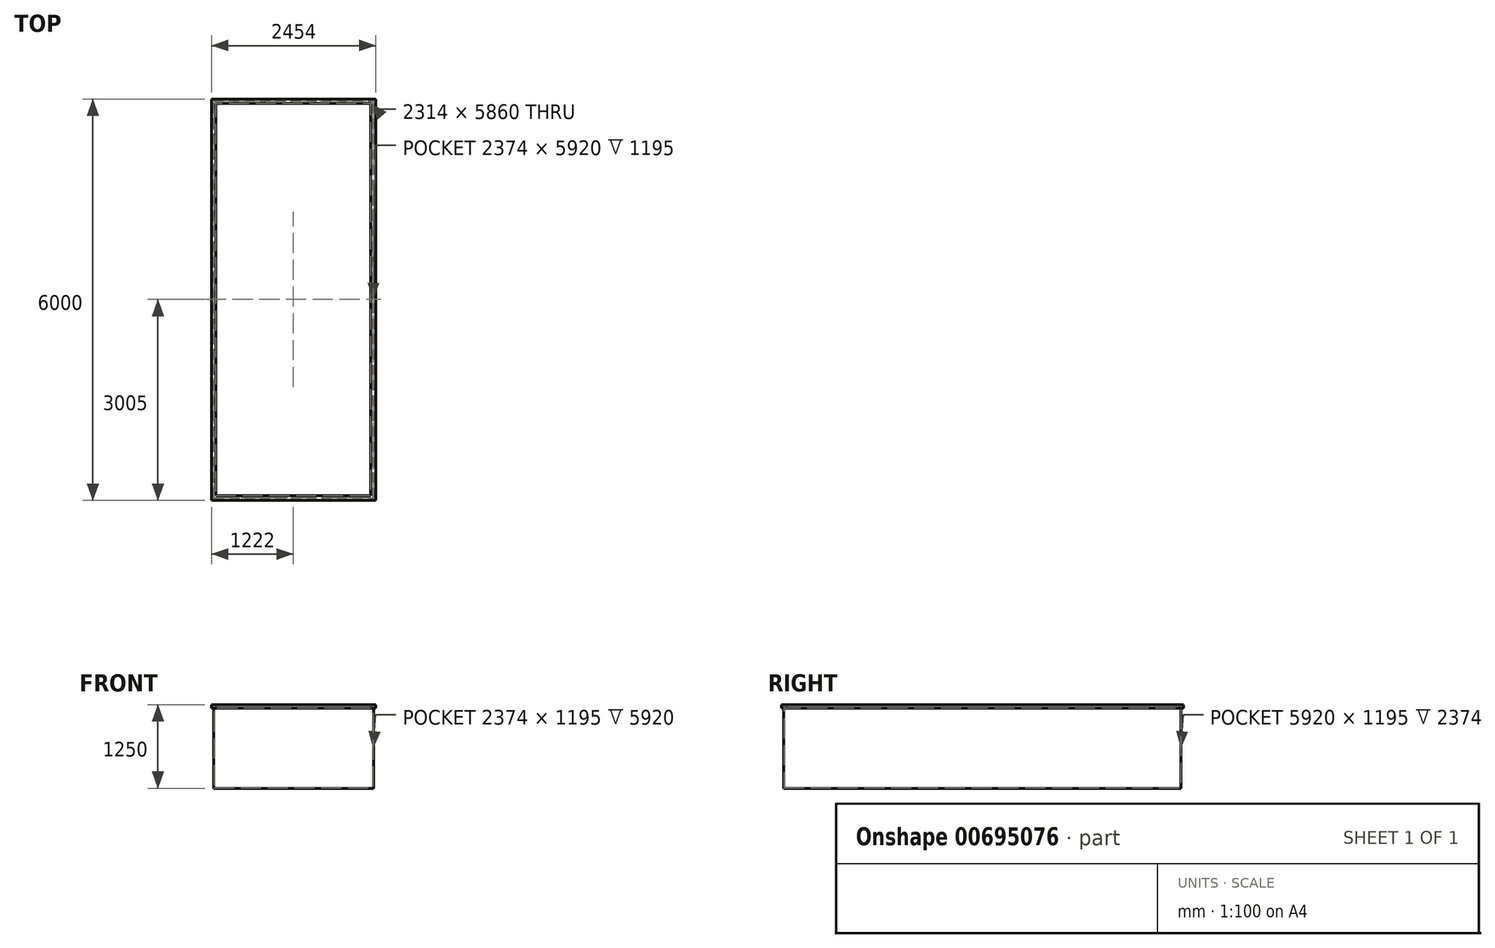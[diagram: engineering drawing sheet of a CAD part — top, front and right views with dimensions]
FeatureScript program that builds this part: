
annotation { "Feature Type Name" : "Feature", "Feature Type Description" : "" }
export const myFeature = defineFeature(function(context is Context, id is Id, definition is map)
    precondition{}
    {
        {
            var Q0;
            Q0=qCreatedBy(makeId("Top.planeOp"),FACE);
            var sketch = newSketch(context, id + "F0", { "sketchPlane" : qUnion([Q0])});
            skLineSegment(sketch, "E0.bottom", {"start": v(0, 0) * mm, "end": v(2384, 0) * mm});
            skLineSegment(sketch, "E0.top", {"start": v(0, 5930) * mm, "end": v(2384, 5930) * mm});
            skLineSegment(sketch, "E0.left", {"start": v(0, 0) * mm, "end": v(0, 5930) * mm});
            skLineSegment(sketch, "E0.right", {"start": v(2384, 0) * mm, "end": v(2384, 5930) * mm});
            skSolve(sketch);
        }
        {
            var Q0;
            Q0=makeQuery(id+"F0.imprint","IMPRINT",FACE,{"disambiguationData":[TD([[makeQuery(id+"F0.imprint","IMPRINT",EDGE,{"derivedFrom":sQuery(id+"F0.wireOp",EDGE,"E0.bottom")}),1.0]])]});
            extrude(context, id + "F1", {"entities" : qUnion([Q0]), "depth" : 1200 * mm, "offsetDistance" : 25 * mm});
        }
        {
            var Q0;
            Q0=makeQuery(id+"F1.opExtrude","CAP_FACE",FACE,{"disambiguationData":[OSD([sQuery(id+"F0.wireOp",EDGE,"E0.bottom"),sQuery(id+"F0.wireOp",EDGE,"E0.top"),sQuery(id+"F0.wireOp",EDGE,"E0.left"),sQuery(id+"F0.wireOp",EDGE,"E0.right")])],"isStart":false});
            shell(context, id + "F2", {"entities" : qUnion([Q0]), "thickness" : 5 * mm});
        }
        {
            var Q0;
            Q0=makeQuery(id+"F1.opExtrude","CAP_FACE",FACE,{"disambiguationData":[OSD([sQuery(id+"F0.wireOp",EDGE,"E0.bottom"),sQuery(id+"F0.wireOp",EDGE,"E0.top"),sQuery(id+"F0.wireOp",EDGE,"E0.left"),sQuery(id+"F0.wireOp",EDGE,"E0.right")])],"isStart":false});
            var sketch = newSketch(context, id + "F3", { "sketchPlane" : qUnion([Q0])});
            skLineSegment(sketch, "E1.bottom", {"start": v(-35, 5965) * mm, "end": v(2419, 5965) * mm});
            skLineSegment(sketch, "E1.top", {"start": v(-35, -35) * mm, "end": v(2419, -35) * mm});
            skLineSegment(sketch, "E1.left", {"start": v(-35, 5965) * mm, "end": v(-35, -35) * mm});
            skLineSegment(sketch, "E1.right", {"start": v(2419, 5965) * mm, "end": v(2419, -35) * mm});
            skLineSegment(sketch, "E2.bottom", {"start": v(30, 5900) * mm, "end": v(2344, 5900) * mm});
            skLineSegment(sketch, "E2.top", {"start": v(30, 40) * mm, "end": v(2344, 40) * mm});
            skLineSegment(sketch, "E2.left", {"start": v(30, 5900) * mm, "end": v(30, 40) * mm});
            skLineSegment(sketch, "E2.right", {"start": v(2344, 5900) * mm, "end": v(2344, 40) * mm});
            skSolve(sketch);
        }
        {
            var Q0;
            Q0=qSketchRegion(id+"F3",true);
            extrude(context, id + "F4", {"entities" : qUnion([Q0]), "operationType" : NewBodyOperationType.ADD, "depth" : 50 * mm, "offsetDistance" : 25 * mm});
        }
    });
